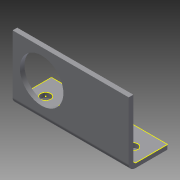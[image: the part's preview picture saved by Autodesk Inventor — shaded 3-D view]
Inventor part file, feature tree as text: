
AUTODESK INVENTOR PART (.ipt)
format: ipt  version: 2013 (Build 170138000, 138)  size: 217,088 bytes
history: native  units: in
note: dims shown in document units (in); Inventor stores cm internally (conversion verified against a paired STEP export)
features: sketch x9, other x7, reference x6, sheet_metal_op x4, extrude x3, projected_geometry x1
ambient origin geometry x8: Origin, YZ Plane, XZ Plane, XY Plane, X Axis, Y Axis, Z Axis, Center Point
bodies: Solid1 (feature_tree)
feature tree (30):
  sheet_metal_op  "Face1"
  sheet_metal_op  "Flange1"
  sketch  "Sketch9"  dims[d9=0.12in]
  sketch  "Sketch10"  dims[d10=0.0in]
  extrude  "Extrusion1"  Depth=1.5in
  extrude  "Extrusion2"  Depth=0.75in
  extrude  "Extrusion3"  Depth=0.75in
  sketch  "Sketch12"  dims[d12=0.06in]
  sketch  "Sketch13"  dims[d13=0.24in d14=0.12in d15=1.0in d16=90.0deg d17=0.05in d18=0.48in d19=0.12in d20=0.12in d32=0.12in d33=0.0in d34=1.5in d35=0.0in d36=1.5in d37=0.0in d38=1.5in d39=0.0in d40=0.12in d41=0.0in d42=0.12in d43=0.0in d5=0.0in]
  sketch  "Sketch1"  dims[d0=1.5in d1=1.5in]
  other  "Plate1"
  sketch  "Sketch2"  dims[d2=0.75in d3=0.75in]
  sketch  "Sketch3"  dims[d4=0.12in d7=0.75in]
  other  "Plate2"
  sheet_metal_op  "Bend1"
  sheet_metal_op  "Corner1"
  sketch  "Sketch8"  dims[d8=1.125in]
  reference  "Reference4"
  reference  "Reference5"
  reference  "Reference6"
  sketch  "Sketch11"  dims[d11=0.12in]
  reference  "Reference7"
  reference  "Reference8"
  projected_geometry  "Projected Loop1"
  reference  "Reference9"
  other  "Cut1"
  other  "Cut5"
  other  "Cut6"
  other  "Cut7"
  other  "Definition1"
